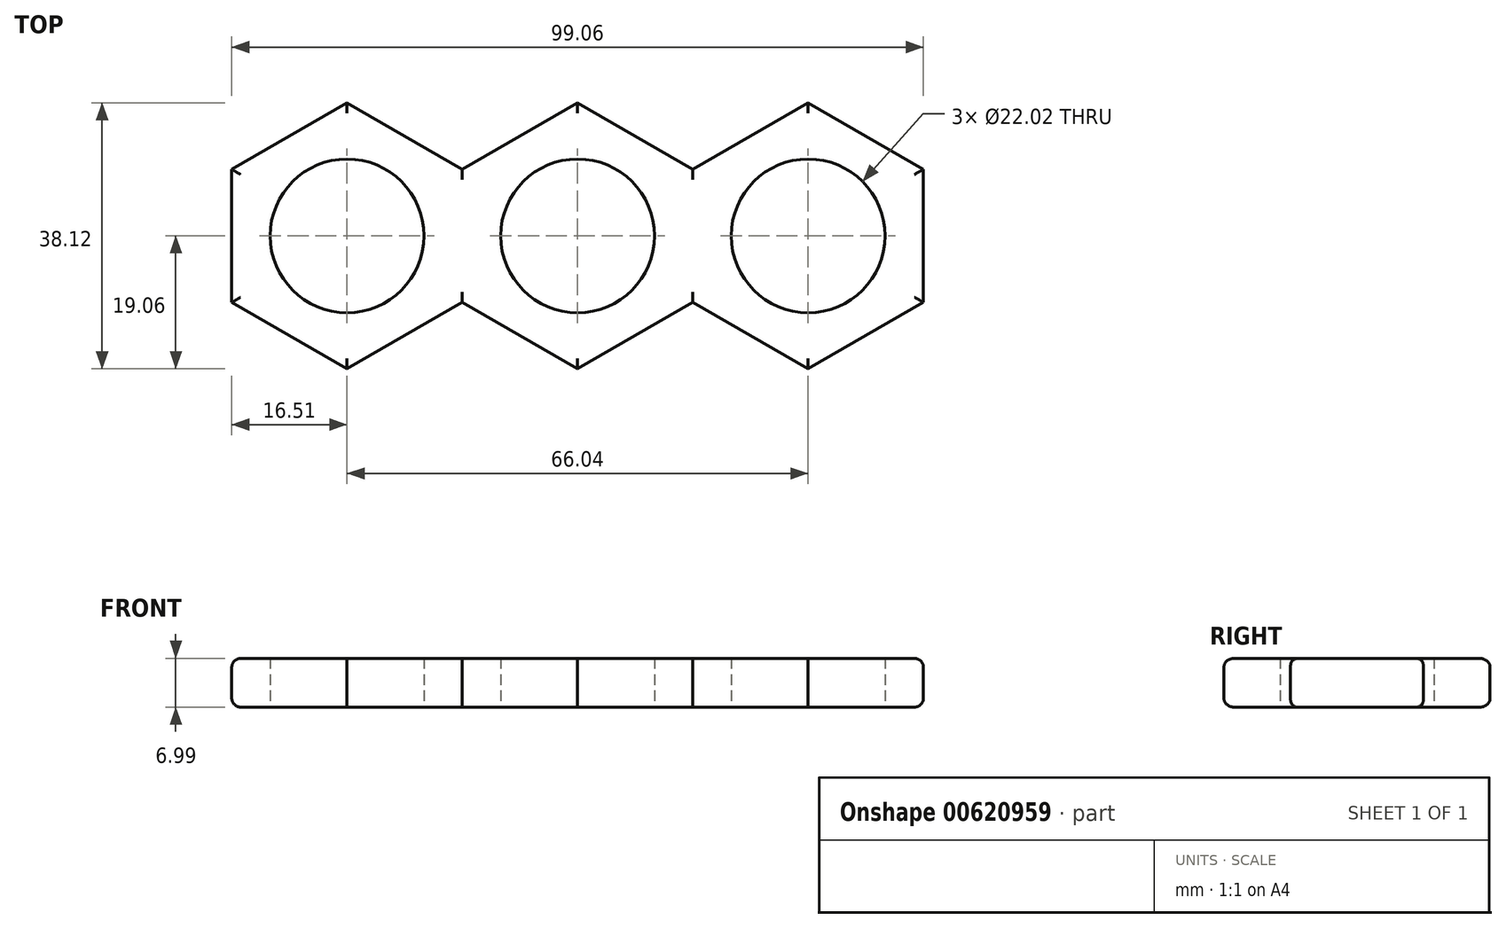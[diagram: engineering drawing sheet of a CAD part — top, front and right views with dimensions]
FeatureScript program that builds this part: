
annotation { "Feature Type Name" : "Feature", "Feature Type Description" : "" }
export const myFeature = defineFeature(function(context is Context, id is Id, definition is map)
    precondition{}
    {
        {
            var Q0;
            Q0=qCreatedBy(makeId("Top.planeOp"),FACE);
            var sketch = newSketch(context, id + "F0", { "sketchPlane" : qUnion([Q0])});
            skCircle(sketch, "E0", {"center": v(0, 0) * mm, "radius": 11.01 * mm});
            skLineSegment(sketch, "E1", {"start": v(0, 0) * mm, "end": v(33.02, 0) * mm});
            skLineSegment(sketch, "E2", {"start": v(33.02, 0) * mm, "end": v(0, 0) * mm});
            skLineSegment(sketch, "E3", {"start": v(-33.02, 0) * mm, "end": v(0, 0) * mm});
            skCircle(sketch, "E4", {"center": v(-33.02, 0) * mm, "radius": 11.01 * mm});
            skCircle(sketch, "E5", {"center": v(33.02, 0) * mm, "radius": 11.01 * mm});
            skCircle(sketch, "E6.cCircle", {"center": v(-33.02, 0) * mm, "radius": 19.06 * mm, "construction": true});
            skLineSegment(sketch, "E6.0", {"start": v(-49.53, -9.53) * mm, "end": v(-49.53, 9.53) * mm});
            skLineSegment(sketch, "E6.1", {"start": v(-49.53, 9.53) * mm, "end": v(-33.02, 19.06) * mm});
            skLineSegment(sketch, "E6.2", {"start": v(-33.02, 19.06) * mm, "end": v(-16.51, 9.53) * mm});
            skLineSegment(sketch, "E6.3", {"start": v(-16.51, 9.53) * mm, "end": v(-16.51, -9.53) * mm});
            skLineSegment(sketch, "E6.4", {"start": v(-16.51, -9.53) * mm, "end": v(-33.02, -19.06) * mm});
            skLineSegment(sketch, "E6.5", {"start": v(-33.02, -19.06) * mm, "end": v(-49.53, -9.53) * mm});
            skCircle(sketch, "E7.cCircle", {"center": v(33.02, 0) * mm, "radius": 19.06 * mm, "construction": true});
            skLineSegment(sketch, "E7.0", {"start": v(49.53, -9.53) * mm, "end": v(33.02, -19.06) * mm});
            skLineSegment(sketch, "E7.1", {"start": v(33.02, -19.06) * mm, "end": v(16.5, -9.53) * mm});
            skLineSegment(sketch, "E7.2", {"start": v(16.5, -9.53) * mm, "end": v(16.5, 9.53) * mm});
            skLineSegment(sketch, "E7.3", {"start": v(16.5, 9.53) * mm, "end": v(33.02, 19.06) * mm});
            skLineSegment(sketch, "E7.4", {"start": v(33.02, 19.06) * mm, "end": v(49.53, 9.53) * mm});
            skLineSegment(sketch, "E7.5", {"start": v(49.53, 9.53) * mm, "end": v(49.53, -9.53) * mm});
            skCircle(sketch, "E8.cCircle", {"center": v(0, 0) * mm, "radius": 19.06 * mm, "construction": true});
            skLineSegment(sketch, "E8.0", {"start": v(16.5, -9.53) * mm, "end": v(0, -19.06) * mm});
            skLineSegment(sketch, "E8.1", {"start": v(0, -19.06) * mm, "end": v(-16.5, -9.53) * mm});
            skLineSegment(sketch, "E8.2", {"start": v(-16.5, -9.53) * mm, "end": v(-16.5, 9.53) * mm});
            skLineSegment(sketch, "E8.3", {"start": v(-16.5, 9.53) * mm, "end": v(0, 19.06) * mm});
            skLineSegment(sketch, "E8.4", {"start": v(0, 19.06) * mm, "end": v(16.5, 9.53) * mm});
            skLineSegment(sketch, "E8.5", {"start": v(16.5, 9.53) * mm, "end": v(16.5, -9.53) * mm});
            skSolve(sketch);
        }
        {
            var Q0;
            Q0 = qSketchRegion(id + "F0", true);
            extrude(context, id + "F1", {"entities" : qUnion([Q0]), "depth" : 7 * mm, "offsetDistance" : 25.4 * mm});
        }
        {
            var Q0;
            Q0=makeQuery(id+"F1.opExtrude","CAP_EDGE",EDGE,{"disambiguationData":[OSD([sQuery(id+"F0.wireOp",EDGE,"E6.1")])],"isStart":false});
            var Q1;
            Q1=makeQuery(id+"F1.opExtrude","CAP_EDGE",EDGE,{"disambiguationData":[OSD([sQuery(id+"F0.wireOp",EDGE,"E6.0")])],"isStart":false});
            var Q2;
            Q2=makeQuery(id+"F1.opExtrude","CAP_EDGE",EDGE,{"disambiguationData":[OSD([sQuery(id+"F0.wireOp",EDGE,"E6.4")])],"isStart":false});
            var Q3;
            Q3=makeQuery(id+"F1.opExtrude","CAP_EDGE",EDGE,{"disambiguationData":[OSD([sQuery(id+"F0.wireOp",EDGE,"E8.1")])],"isStart":false});
            var Q4;
            Q4=makeQuery(id+"F1.opExtrude","CAP_EDGE",EDGE,{"disambiguationData":[OSD([sQuery(id+"F0.wireOp",EDGE,"E8.0")])],"isStart":false});
            var Q5;
            Q5=makeQuery(id+"F1.opExtrude","CAP_EDGE",EDGE,{"disambiguationData":[OSD([sQuery(id+"F0.wireOp",EDGE,"E7.1")])],"isStart":false});
            var Q6;
            Q6=makeQuery(id+"F1.opExtrude","CAP_EDGE",EDGE,{"disambiguationData":[OSD([sQuery(id+"F0.wireOp",EDGE,"E7.0")])],"isStart":false});
            var Q7;
            Q7=makeQuery(id+"F1.opExtrude","CAP_EDGE",EDGE,{"disambiguationData":[OSD([sQuery(id+"F0.wireOp",EDGE,"E7.5")])],"isStart":false});
            var Q8;
            Q8=makeQuery(id+"F1.opExtrude","CAP_EDGE",EDGE,{"disambiguationData":[OSD([sQuery(id+"F0.wireOp",EDGE,"E7.4")])],"isStart":false});
            var Q9;
            Q9=makeQuery(id+"F1.opExtrude","CAP_EDGE",EDGE,{"disambiguationData":[OSD([sQuery(id+"F0.wireOp",EDGE,"E7.3")])],"isStart":false});
            var Q10;
            Q10=makeQuery(id+"F1.opExtrude","CAP_EDGE",EDGE,{"disambiguationData":[OSD([sQuery(id+"F0.wireOp",EDGE,"E8.4")])],"isStart":false});
            var Q11;
            Q11=makeQuery(id+"F1.opExtrude","CAP_EDGE",EDGE,{"disambiguationData":[OSD([sQuery(id+"F0.wireOp",EDGE,"E8.3")])],"isStart":false});
            var Q12;
            Q12=makeQuery(id+"F1.opExtrude","CAP_EDGE",EDGE,{"disambiguationData":[OSD([sQuery(id+"F0.wireOp",EDGE,"E6.2")])],"isStart":false});
            var Q13;
            Q13=makeQuery(id+"F1.opExtrude","CAP_EDGE",EDGE,{"disambiguationData":[OSD([sQuery(id+"F0.wireOp",EDGE,"E6.5")])],"isStart":false});
            var Q14;
            Q14=makeQuery(id+"F1.opExtrude","CAP_EDGE",EDGE,{"disambiguationData":[OSD([sQuery(id+"F0.wireOp",EDGE,"E6.0")])],"isStart":true});
            var Q15;
            Q15=makeQuery(id+"F1.opExtrude","CAP_EDGE",EDGE,{"disambiguationData":[OSD([sQuery(id+"F0.wireOp",EDGE,"E6.5")])],"isStart":true});
            var Q16;
            Q16=makeQuery(id+"F1.opExtrude","CAP_EDGE",EDGE,{"disambiguationData":[OSD([sQuery(id+"F0.wireOp",EDGE,"E6.4")])],"isStart":true});
            var Q17;
            Q17=makeQuery(id+"F1.opExtrude","CAP_EDGE",EDGE,{"disambiguationData":[OSD([sQuery(id+"F0.wireOp",EDGE,"E8.1")])],"isStart":true});
            var Q18;
            Q18=makeQuery(id+"F1.opExtrude","CAP_EDGE",EDGE,{"disambiguationData":[OSD([sQuery(id+"F0.wireOp",EDGE,"E7.1")])],"isStart":true});
            var Q19;
            Q19=makeQuery(id+"F1.opExtrude","CAP_EDGE",EDGE,{"disambiguationData":[OSD([sQuery(id+"F0.wireOp",EDGE,"E8.0")])],"isStart":true});
            var Q20;
            Q20=makeQuery(id+"F1.opExtrude","CAP_EDGE",EDGE,{"disambiguationData":[OSD([sQuery(id+"F0.wireOp",EDGE,"E7.0")])],"isStart":true});
            var Q21;
            Q21=makeQuery(id+"F1.opExtrude","CAP_EDGE",EDGE,{"disambiguationData":[OSD([sQuery(id+"F0.wireOp",EDGE,"E7.5")])],"isStart":true});
            var Q22;
            Q22=makeQuery(id+"F1.opExtrude","CAP_EDGE",EDGE,{"disambiguationData":[OSD([sQuery(id+"F0.wireOp",EDGE,"E7.4")])],"isStart":true});
            var Q23;
            Q23=makeQuery(id+"F1.opExtrude","CAP_EDGE",EDGE,{"disambiguationData":[OSD([sQuery(id+"F0.wireOp",EDGE,"E7.3")])],"isStart":true});
            var Q24;
            Q24=makeQuery(id+"F1.opExtrude","CAP_EDGE",EDGE,{"disambiguationData":[OSD([sQuery(id+"F0.wireOp",EDGE,"E8.4")])],"isStart":true});
            var Q25;
            Q25=makeQuery(id+"F1.opExtrude","CAP_EDGE",EDGE,{"disambiguationData":[OSD([sQuery(id+"F0.wireOp",EDGE,"E8.3")])],"isStart":true});
            var Q26;
            Q26=makeQuery(id+"F1.opExtrude","CAP_EDGE",EDGE,{"disambiguationData":[OSD([sQuery(id+"F0.wireOp",EDGE,"E6.2")])],"isStart":true});
            var Q27;
            Q27=makeQuery(id+"F1.opExtrude","CAP_EDGE",EDGE,{"disambiguationData":[OSD([sQuery(id+"F0.wireOp",EDGE,"E6.1")])],"isStart":true});
            fillet(context, id + "F2", {"entities" : qUnion([Q0, Q1, Q2, Q3, Q4, Q5, Q6, Q7, Q8, Q9, Q10, Q11, Q12, Q13, Q14, Q15, Q16, Q17, Q18, Q19, Q20, Q21, Q22, Q23, Q24, Q25, Q26, Q27]), "radius" : 1.27 * mm, "tangentPropagation" : true, "allowEdgeOverflow" : false});
        }
    });
